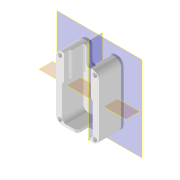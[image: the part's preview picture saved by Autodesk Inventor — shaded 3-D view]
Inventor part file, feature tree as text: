
AUTODESK INVENTOR PART (.ipt)
format: ipt  version: 2022 (Build 260153000, 153)  size: 561,152 bytes
history: native  units: mm
features: reference x23, sketch x13, other x12, extrude x11, projected_geometry x8, plane x5, fillet x4, hole x3, chamfer x1
ambient origin geometry x8: Origin, YZ Plane, XZ Plane, XY Plane, X Axis, Y Axis, Z Axis, Center Point
bodies: Solid1 (feature_tree)
feature tree (80):
  plane  "Work Plane1"
  extrude  "Extrusion1"  Depth=53.8mm
  extrude  "IM_offset"  Depth=53.8mm
  plane  "Arbeitsebene5"
  plane  "Arbeitsebene6"
  extrude  "Extrusion26"  Depth=45.0mm
  chamfer  "Fase2"  Distance=0.2mm
  plane  "Arbeitsebene9"
  extrude  "Extrusion29"  Depth=10.0mm TaperAngle=0.0deg
  extrude  "Extrusion30"  Depth=2.0mm
  plane  "Arbeitsebene10"
  extrude  "Extrusion31"  Depth=10.0mm TaperAngle=0.0deg
  fillet  "Rundung3"  Radius=2.0mm
  hole  "Bohrung2"  [1 undecoded]
  extrude  "Extrusion32"  Depth=2.0mm
  hole  "Bohrung3"  [1 undecoded]
  extrude  "Extrusion33"  TaperAngle=0.0deg  [1 undecoded]
  extrude  "Extrusion34"  Depth=10.0mm TaperAngle=0.0deg
  extrude  "Extrusion35"  Depth=2.0mm
  fillet  "Rundung5"  Radius=12.0mm
  hole  "Bohrung4"  [1 undecoded]
  fillet  "Rundung6"  Radius=30.0mm
  extrude  "Extrusion36"  Depth=2.0mm
  fillet  "Rundung7"  [1 undecoded]
  sketch  "Sketch1"  dims[d10=12.0mm d11=0.0mm d18=53.8mm]
  reference  "Reference1"
  reference  "Reference2"
  reference  "Reference3"
  reference  "Reference4"
  reference  "Reference9"
  reference  "Reference20"
  reference  "Reference21"
  reference  "Reference22"
  reference  "Reference23"
  reference  "Reference24"
  sketch  "Skizze4"  dims[d19=45.0deg d20=53.8mm]
  projected_geometry  "Projizierte Kontur1"
  sketch  "Skizze31"  dims[d21=45.0mm d22=45.0mm]
  projected_geometry  "Projizierte Kontur17"
  sketch  "Skizze34"  dims[d30=20.0mm]
  reference  "Referenz35"
  sketch  "Skizze35"  dims[d31=20.0mm]
  reference  "Referenz36"
  reference  "Referenz37"
  reference  "Referenz38"
  reference  "Referenz39"
  reference  "Referenz40"
  sketch  "Skizze37"  dims[d32=2.8mm]
  projected_geometry  "Projizierte Kontur18"
  reference  "Referenz41"
  sketch  "Skizze38"  dims[d33=2.8mm]
  reference  "Referenz42"
  sketch  "Skizze39"  dims[d34=2.8mm]
  reference  "Referenz43"
  sketch  "Skizze40"  dims[d35=3.0mm]
  projected_geometry  "Projizierte Kontur19"
  sketch  "Skizze41"  dims[d36=0.1mm]
  projected_geometry  "Projizierte Kontur20"
  sketch  "Skizze42"  dims[d37=0.1mm]
  projected_geometry  "Projizierte Kontur21"
  projected_geometry  "Projizierte Kontur22"
  sketch  "Skizze43"  dims[d38=0.1mm]
  reference  "Referenz44"
  reference  "Referenz45"
  reference  "Referenz46"
  reference  "Referenz47"
  sketch  "Skizze44"  dims[d39=0.1mm d40=0.2mm d41=10.0mm d42=0.0mm d181=7.5mm d182=10.0mm d183=0.0mm d184=0.5mm d185=2.0mm d186=45.0deg d193=-1.5mm d194=8.6mm d195=8.6mm d196=0.0mm d197=0.0mm d198=10.0mm d199=0.0mm d200=4.0mm d201=12.0mm d202=0.0mm d203=1.0mm d204=30.0mm d205=30.0mm d206=2.8mm d207=6.0mm d208=8.0mm d209=6.0mm d210=90.0deg d211=8.0mm d212=20.594885mm d213=0.0mm d214=0.0mm d215=2.8mm d216=6.0mm d217=4.0mm d218=2.0mm d219=90.0deg d220=8.0mm d221=20.594885mm d222=2.0mm d223=0.0mm d224=1.0mm d225=7.0mm d226=10.0mm d227=0.0mm d229=1.5mm d230=0.0mm d231=2.0mm d232=2.8mm d233=6.0mm d234=4.0mm d235=2.0mm d236=90.0deg d237=8.0mm d238=20.594885mm d239=4.0mm d240=12.0mm d241=24.0mm d242=2.0mm d243=10.0mm d244=0.0mm d245=2.0mm d160=0.5mm d161=0.872665mm d162=0.5mm d163=0.872665mm]
  projected_geometry  "Projizierte Kontur23"
  other  "Assembly_Cube_v2_Thorlabs.iam"
  other  "10_Cube_Base:1"
  other  "00_Base_v0:1"
  other  "Assembly_Cube_Kinematic_Mirrormount_v2.iam"
  other  "Assembly_Cube_empty_1x1_v2:1"
  other  "10_Cube_1x1_v2:1"
  other  "10_Lid_1x1_v2:1"
  other  "Assembly_Cube_SEEED_Xiao_Sense_Camera_adapter_v3.iam"
  other  "00_Seeeduino Xiao:1"
  other  "00_ESP3-CAM:1"
  other  "00_ESP32_XIAO_Adapter_lid:1"
  other  "10_Cube_Lid:1"
note: 5 required parameter values undecoded (feature->parameter linkage not recoverable at this tier; creation-order binding heuristic only, values carry confidence <= 0.55)
